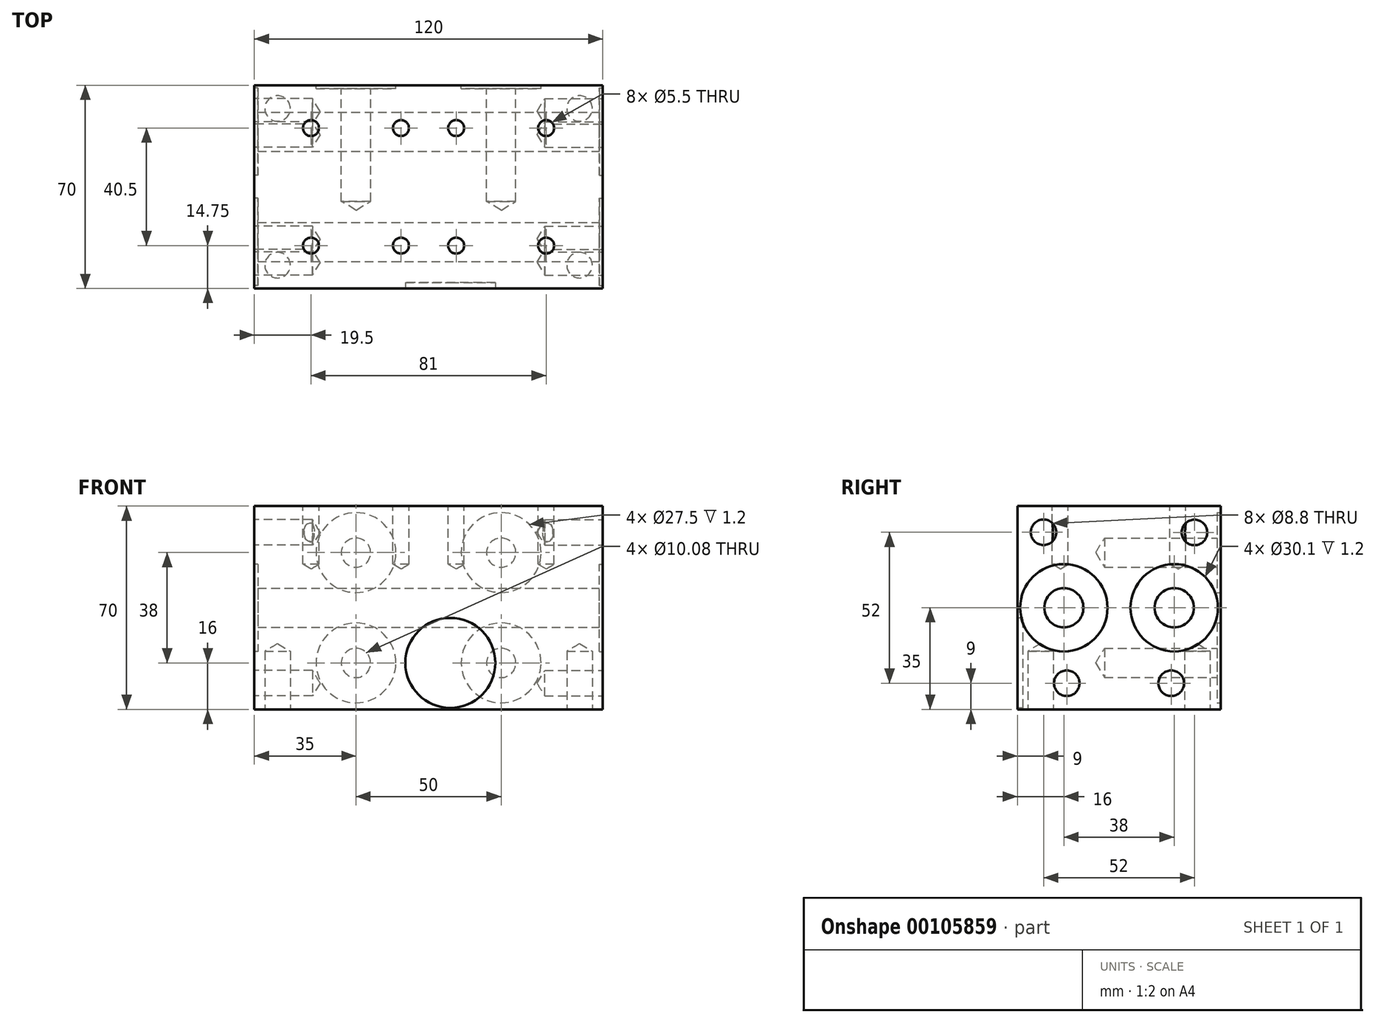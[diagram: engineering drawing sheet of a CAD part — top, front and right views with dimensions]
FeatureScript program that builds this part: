
annotation { "Feature Type Name" : "Feature", "Feature Type Description" : "" }
export const myFeature = defineFeature(function(context is Context, id is Id, definition is map)
    precondition{}
    {
        {
            var Q0;
            Q0=qCreatedBy(makeId("Right.planeOp"),FACE);
            var sketch = newSketch(context, id + "F0", { "sketchPlane" : qUnion([Q0])});
            skLineSegment(sketch, "E0.bottom", {"start": v(-35, -35) * mm, "end": v(35, -35) * mm});
            skLineSegment(sketch, "E0.top", {"start": v(-35, 35) * mm, "end": v(35, 35) * mm});
            skLineSegment(sketch, "E0.left", {"start": v(-35, -35) * mm, "end": v(-35, 35) * mm});
            skLineSegment(sketch, "E0.right", {"start": v(35, -35) * mm, "end": v(35, 35) * mm});
            skPoint(sketch, "E0.middle", {"position": v(0, 0) * mm});
            skSolve(sketch);
        }
        {
            var Q0;
            Q0=makeQuery(id+"F0.imprint","IMPRINT",FACE,{"disambiguationData":[TD([[makeQuery(id+"F0.imprint","IMPRINT",EDGE,{"derivedFrom":sQuery(id+"F0.wireOp",EDGE,"E0.bottom")}),1.0]])]});
            extrude(context, id + "F1", {"entities" : qUnion([Q0]), "depth" : 120 * mm});
        }
        {
            var Q0;
            Q0=makeQuery(id+"F1.opExtrude","CAP_FACE",FACE,{"disambiguationData":[OSD([sQuery(id+"F0.wireOp",EDGE,"E0.bottom"),sQuery(id+"F0.wireOp",EDGE,"E0.top"),sQuery(id+"F0.wireOp",EDGE,"E0.left"),sQuery(id+"F0.wireOp",EDGE,"E0.right")])],"isStart":false});
            var sketch = newSketch(context, id + "F2", { "sketchPlane" : qUnion([Q0])});
            skPoint(sketch, "E1", {"position": v(18, -26) * mm});
            skPoint(sketch, "E2", {"position": v(-18, -26) * mm});
            skPoint(sketch, "E3", {"position": v(-26, 26) * mm});
            skPoint(sketch, "E4", {"position": v(26, 25.94) * mm});
            skCircle(sketch, "E5", {"center": v(-19, 0) * mm, "radius": 15.05 * mm});
            skCircle(sketch, "E6", {"center": v(19, 0) * mm, "radius": 15.05 * mm});
            skSolve(sketch);
        }
        {
            var Q0;
            Q0=sQuery(id+"F2.wireOp",VERTEX,"E5.center");
            var Q1;
            Q1=sQuery(id+"F2.wireOp",VERTEX,"E6.center");
            var Q2;
            Q2=makeQuery(id+"F1.opExtrude","SWEPT_BODY",BODY,{"disambiguationData":[OSD([sQuery(id+"F0.wireOp",EDGE,"E0.bottom"),sQuery(id+"F0.wireOp",EDGE,"E0.top"),sQuery(id+"F0.wireOp",EDGE,"E0.left"),sQuery(id+"F0.wireOp",EDGE,"E0.right")])]});
            hole(context, id + "F3", {"style" : HoleStyle.SIMPLE, "endStyle" : HoleEndStyle.THROUGH, "standardTappedOrClearance" : lookupTablePath({ "standard" : "ANSI", "fit" : "Normal (ASME)", "size" : "1/2", "type" : "Clearance" }), "standardBlindInLast" : lookupTablePath({ "fit" : "Free", "standard" : "ANSI", "size" : "1/2", "type" : "Clearance" }), "holeDiameter" : 13.5 * mm, "locations" : qUnion([Q0, Q1]), "scope" : qUnion([Q2]), "isTappedThrough" : true});
        }
        {
            var Q0;
            Q0=sQuery(id+"F2.wireOp",VERTEX,"E3");
            var Q1;
            Q1=sQuery(id+"F2.wireOp",VERTEX,"E4");
            var Q2;
            Q2=sQuery(id+"F2.wireOp",VERTEX,"E2");
            var Q3;
            Q3=sQuery(id+"F2.wireOp",VERTEX,"E1");
            var Q4;
            Q4=makeQuery(id+"F1.opExtrude","SWEPT_BODY",BODY,{"disambiguationData":[OSD([sQuery(id+"F0.wireOp",EDGE,"E0.bottom"),sQuery(id+"F0.wireOp",EDGE,"E0.top"),sQuery(id+"F0.wireOp",EDGE,"E0.left"),sQuery(id+"F0.wireOp",EDGE,"E0.right")])]});
            hole(context, id + "F4", {"style" : HoleStyle.SIMPLE, "endStyle" : HoleEndStyle.BLIND, "standardTappedOrClearance" : lookupTablePath({ "standard" : "ISO", "fit" : "Normal", "size" : "M8", "type" : "Clearance" }), "standardBlindInLast" : lookupTablePath({ "fit" : "Standard", "standard" : "ISO", "size" : "M8", "type" : "Clearance" }), "holeDiameter" : 8.8 * mm, "holeDepth" : 20 * mm, "locations" : qUnion([Q0, Q1, Q2, Q3]), "scope" : qUnion([Q4])});
        }
        {
            var Q0;
            Q0 = qSketchRegion(id + "F2", true);
            extrude(context, id + "F5", {"entities" : qUnion([Q0]), "operationType" : NewBodyOperationType.REMOVE, "oppositeDirection" : true, "depth" : 1.2 * mm});
        }
        {
            var Q0;
            Q0=makeQuery(id+"F1.opExtrude","CAP_FACE",FACE,{"disambiguationData":[OSD([sQuery(id+"F0.wireOp",EDGE,"E0.bottom"),sQuery(id+"F0.wireOp",EDGE,"E0.top"),sQuery(id+"F0.wireOp",EDGE,"E0.left"),sQuery(id+"F0.wireOp",EDGE,"E0.right")])],"isStart":true});
            var sketch = newSketch(context, id + "F6", { "sketchPlane" : qUnion([Q0])});
            skPoint(sketch, "E7", {"position": v(18, -26) * mm});
            skPoint(sketch, "E8", {"position": v(-18, -26) * mm});
            skPoint(sketch, "E9", {"position": v(-26, 25.94) * mm});
            skPoint(sketch, "E10", {"position": v(26, 26) * mm});
            skCircle(sketch, "E11", {"center": v(-19, 0) * mm, "radius": 15.05 * mm});
            skCircle(sketch, "E12", {"center": v(19, 0) * mm, "radius": 15.05 * mm});
            skSolve(sketch);
        }
        {
            var Q0;
            Q0=sQuery(id+"F6.wireOp",VERTEX,"E9");
            var Q1;
            Q1=sQuery(id+"F6.wireOp",VERTEX,"E10");
            var Q2;
            Q2=sQuery(id+"F6.wireOp",VERTEX,"E8");
            var Q3;
            Q3=sQuery(id+"F6.wireOp",VERTEX,"E7");
            var Q4;
            Q4=makeQuery(id+"F1.opExtrude","SWEPT_BODY",BODY,{"disambiguationData":[OSD([sQuery(id+"F0.wireOp",EDGE,"E0.bottom"),sQuery(id+"F0.wireOp",EDGE,"E0.top"),sQuery(id+"F0.wireOp",EDGE,"E0.left"),sQuery(id+"F0.wireOp",EDGE,"E0.right")])]});
            hole(context, id + "F7", {"style" : HoleStyle.SIMPLE, "endStyle" : HoleEndStyle.BLIND, "standardTappedOrClearance" : lookupTablePath({ "standard" : "ISO", "fit" : "Normal", "size" : "M8", "type" : "Clearance" }), "standardBlindInLast" : lookupTablePath({ "fit" : "Standard", "standard" : "ISO", "size" : "M8", "type" : "Clearance" }), "holeDiameter" : 8.8 * mm, "holeDepth" : 20 * mm, "locations" : qUnion([Q0, Q1, Q2, Q3]), "scope" : qUnion([Q4])});
        }
        {
            var Q0;
            Q0 = qSketchRegion(id + "F6", true);
            extrude(context, id + "F8", {"entities" : qUnion([Q0]), "operationType" : NewBodyOperationType.REMOVE, "oppositeDirection" : true, "depth" : 1.2 * mm});
        }
        {
            var Q0;
            Q0=makeQuery(id+"F1.opExtrude","SWEPT_FACE",FACE,{"disambiguationData":[OSD([sQuery(id+"F0.wireOp",EDGE,"E0.top")])]});
            var sketch = newSketch(context, id + "F9", { "sketchPlane" : qUnion([Q0])});
            skPoint(sketch, "E13", {"position": v(168.59, 0) * mm});
            skPoint(sketch, "E14", {"position": v(19.5, 20.25) * mm});
            skPoint(sketch, "E15", {"position": v(19.5, -20.25) * mm});
            skPoint(sketch, "E16", {"position": v(50.5, -20.25) * mm});
            skPoint(sketch, "E17", {"position": v(50.5, 20.25) * mm});
            skPoint(sketch, "E18.1.0.0", {"position": v(69.5, 20.25) * mm});
            skPoint(sketch, "E18.1.0.1", {"position": v(69.5, -20.25) * mm});
            skPoint(sketch, "E18.1.0.2", {"position": v(100.5, -20.25) * mm});
            skPoint(sketch, "E18.1.0.3", {"position": v(100.5, 20.25) * mm});
            skLineSegment(sketch, "E18.direction1", {"start": v(19.5, 20.25) * mm, "end": v(69.5, 20.25) * mm, "construction": true});
            skSolve(sketch);
        }
        {
            var Q0;
            Q0=sQuery(id+"F9.wireOp",VERTEX,"E14");
            var Q1;
            Q1=sQuery(id+"F9.wireOp",VERTEX,"E15");
            var Q2;
            Q2=sQuery(id+"F9.wireOp",VERTEX,"E16");
            var Q3;
            Q3=sQuery(id+"F9.wireOp",VERTEX,"E17");
            var Q4;
            Q4=sQuery(id+"F9.wireOp",VERTEX,"E18.1.0.0");
            var Q5;
            Q5=sQuery(id+"F9.wireOp",VERTEX,"E18.1.0.1");
            var Q6;
            Q6=sQuery(id+"F9.wireOp",VERTEX,"E18.1.0.2");
            var Q7;
            Q7=sQuery(id+"F9.wireOp",VERTEX,"E18.1.0.3");
            var Q8;
            Q8=makeQuery(id+"F1.opExtrude","SWEPT_BODY",BODY,{"disambiguationData":[OSD([sQuery(id+"F0.wireOp",EDGE,"E0.bottom"),sQuery(id+"F0.wireOp",EDGE,"E0.top"),sQuery(id+"F0.wireOp",EDGE,"E0.left"),sQuery(id+"F0.wireOp",EDGE,"E0.right")])]});
            hole(context, id + "F10", {"style" : HoleStyle.SIMPLE, "endStyle" : HoleEndStyle.BLIND, "standardTappedOrClearance" : lookupTablePath({ "standard" : "ISO", "fit" : "Normal", "size" : "M5", "type" : "Clearance" }), "standardBlindInLast" : lookupTablePath({ "fit" : "Standard", "standard" : "ISO", "size" : "M5", "type" : "Clearance" }), "holeDiameter" : 5.5 * mm, "holeDepth" : 20 * mm, "locations" : qUnion([Q0, Q1, Q2, Q3, Q4, Q5, Q6, Q7]), "scope" : qUnion([Q8])});
        }
        {
            var Q0;
            Q0=makeQuery(id+"F1.opExtrude","SWEPT_FACE",FACE,{"disambiguationData":[OSD([sQuery(id+"F0.wireOp",EDGE,"E0.bottom")])]});
            var sketch = newSketch(context, id + "F11", { "sketchPlane" : qUnion([Q0])});
            skPoint(sketch, "E19", {"position": v(8, 27) * mm});
            skPoint(sketch, "E20", {"position": v(8, -27) * mm});
            skPoint(sketch, "E21", {"position": v(112, 27) * mm});
            skPoint(sketch, "E22", {"position": v(112, -27) * mm});
            skSolve(sketch);
        }
        {
            var Q0;
            Q0=sQuery(id+"F11.wireOp",VERTEX,"E19");
            var Q1;
            Q1=sQuery(id+"F11.wireOp",VERTEX,"E20");
            var Q2;
            Q2=sQuery(id+"F11.wireOp",VERTEX,"E21");
            var Q3;
            Q3=sQuery(id+"F11.wireOp",VERTEX,"E22");
            var Q4;
            Q4=makeQuery(id+"F1.opExtrude","SWEPT_BODY",BODY,{"disambiguationData":[OSD([sQuery(id+"F0.wireOp",EDGE,"E0.bottom"),sQuery(id+"F0.wireOp",EDGE,"E0.top"),sQuery(id+"F0.wireOp",EDGE,"E0.left"),sQuery(id+"F0.wireOp",EDGE,"E0.right")])]});
            hole(context, id + "F12", {"style" : HoleStyle.SIMPLE, "endStyle" : HoleEndStyle.BLIND, "standardTappedOrClearance" : lookupTablePath({ "standard" : "ISO", "fit" : "Normal", "size" : "M8", "type" : "Clearance" }), "standardBlindInLast" : lookupTablePath({ "fit" : "Standard", "standard" : "ISO", "size" : "M8", "type" : "Clearance" }), "holeDiameter" : 8.8 * mm, "holeDepth" : 20 * mm, "locations" : qUnion([Q0, Q1, Q2, Q3]), "scope" : qUnion([Q4])});
        }
        {
            var Q0;
            Q0=makeQuery(id+"F1.opExtrude","SWEPT_FACE",FACE,{"disambiguationData":[OSD([sQuery(id+"F0.wireOp",EDGE,"E0.right")])]});
            var sketch = newSketch(context, id + "F13", { "sketchPlane" : qUnion([Q0])});
            skPoint(sketch, "E23", {"position": v(-85, 19) * mm});
            skPoint(sketch, "E24", {"position": v(-85, -19) * mm});
            skPoint(sketch, "E25", {"position": v(-35, 19) * mm});
            skPoint(sketch, "E26", {"position": v(-35, -19) * mm});
            skCircle(sketch, "E27", {"center": v(-85, 19) * mm, "radius": 13.75 * mm});
            skCircle(sketch, "E28.0.1.0", {"center": v(-85, -19) * mm, "radius": 13.75 * mm});
            skCircle(sketch, "E28.1.0.0", {"center": v(-35, 19) * mm, "radius": 13.75 * mm});
            skCircle(sketch, "E28.1.1.0", {"center": v(-35, -19) * mm, "radius": 13.75 * mm});
            skLineSegment(sketch, "E28.direction1", {"start": v(-85, 19) * mm, "end": v(-35, 19) * mm, "construction": true});
            skLineSegment(sketch, "E28.direction2", {"start": v(-85, 19) * mm, "end": v(-85, -19) * mm, "construction": true});
            skSolve(sketch);
        }
        {
            var Q0;
            Q0=sQuery(id+"F13.wireOp",VERTEX,"E23");
            var Q1;
            Q1=sQuery(id+"F13.wireOp",VERTEX,"E25");
            var Q2;
            Q2=sQuery(id+"F13.wireOp",VERTEX,"E26");
            var Q3;
            Q3=sQuery(id+"F13.wireOp",VERTEX,"E24");
            var Q4;
            Q4=makeQuery(id+"F1.opExtrude","SWEPT_BODY",BODY,{"disambiguationData":[OSD([sQuery(id+"F0.wireOp",EDGE,"E0.bottom"),sQuery(id+"F0.wireOp",EDGE,"E0.top"),sQuery(id+"F0.wireOp",EDGE,"E0.left"),sQuery(id+"F0.wireOp",EDGE,"E0.right")])]});
            hole(context, id + "F14", {"style" : HoleStyle.SIMPLE, "endStyle" : HoleEndStyle.BLIND, "standardTappedOrClearance" : lookupTablePath({ "standard" : "ANSI", "fit" : "Normal (ASME)", "size" : "3/8", "type" : "Clearance" }), "standardBlindInLast" : lookupTablePath({ "fit" : "Free", "standard" : "ANSI", "size" : "3/8", "type" : "Clearance" }), "holeDiameter" : 10.08 * mm, "holeDepth" : 40 * mm, "locations" : qUnion([Q0, Q1, Q2, Q3]), "scope" : qUnion([Q4])});
        }
        {
            var Q0;
            Q0 = qSketchRegion(id + "F13", true);
            extrude(context, id + "F15", {"entities" : qUnion([Q0]), "operationType" : NewBodyOperationType.REMOVE, "oppositeDirection" : true, "depth" : 1.2 * mm});
        }
        {
            var Q0;
            Q0=makeQuery(id+"F1.opExtrude","SWEPT_FACE",FACE,{"disambiguationData":[OSD([sQuery(id+"F0.wireOp",EDGE,"E0.left")])]});
            var sketch = newSketch(context, id + "F16", { "sketchPlane" : qUnion([Q0])});
            skCircle(sketch, "E29", {"center": v(67.5, -19) * mm, "radius": 15.5 * mm});
            skSolve(sketch);
        }
        {
            var Q0;
            Q0 = qSketchRegion(id + "F16", true);
            extrude(context, id + "F17", {"entities" : qUnion([Q0]), "operationType" : NewBodyOperationType.REMOVE, "oppositeDirection" : true, "depth" : 2 * mm});
        }
    });
